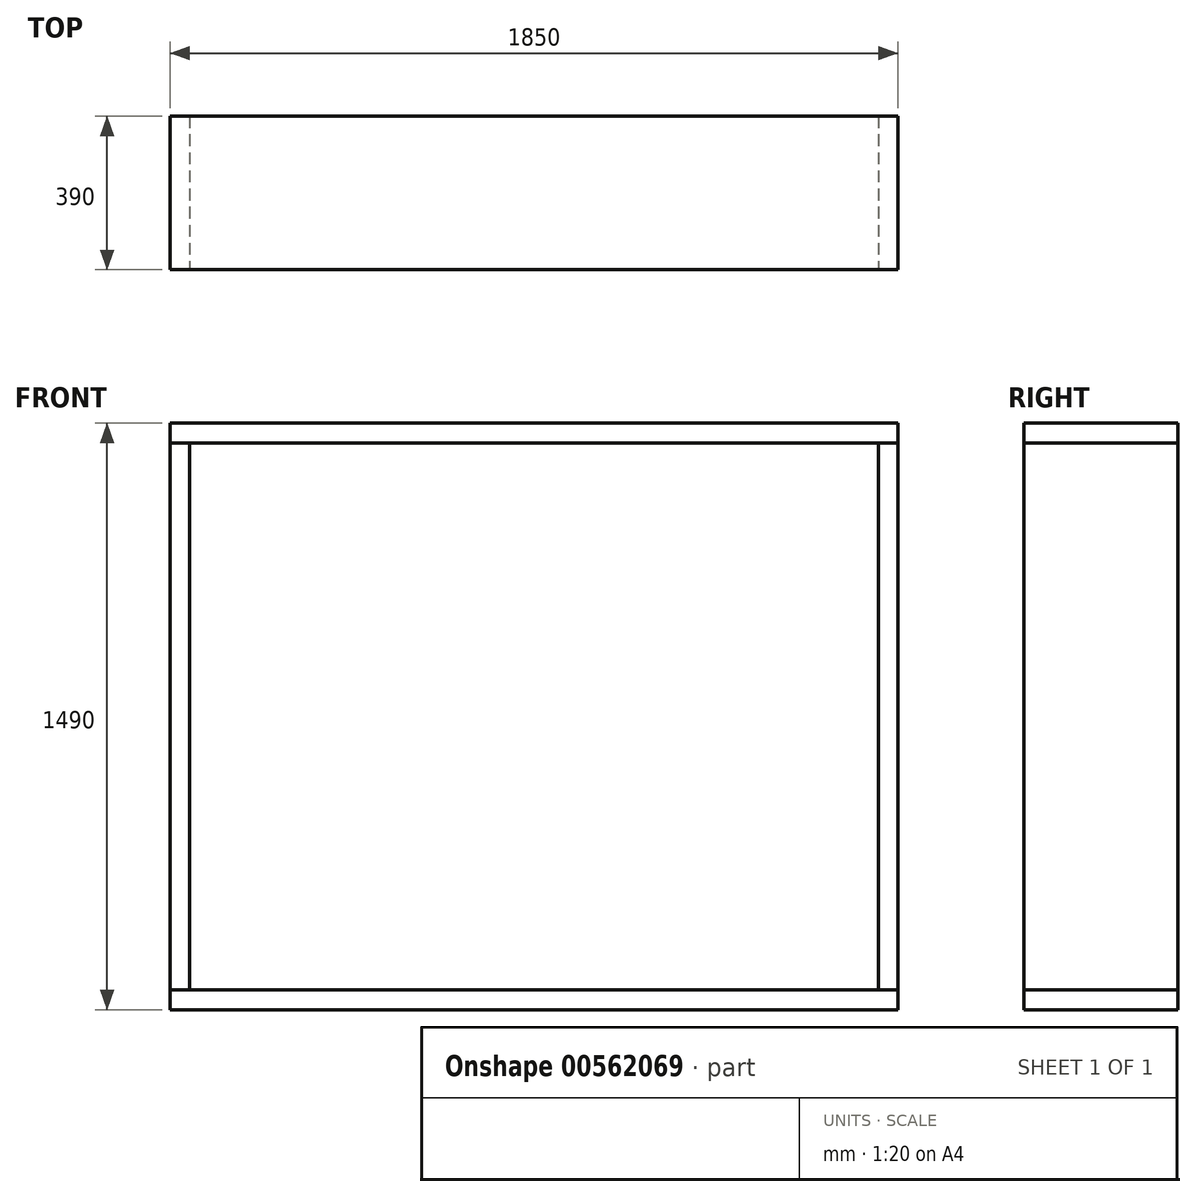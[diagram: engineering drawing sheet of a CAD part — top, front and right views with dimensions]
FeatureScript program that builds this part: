
annotation { "Feature Type Name" : "Feature", "Feature Type Description" : "" }
export const myFeature = defineFeature(function(context is Context, id is Id, definition is map)
    precondition{}
    {
        {
            var Q0;
            Q0=qCreatedBy(makeId("Top.planeOp"),FACE);
            var sketch = newSketch(context, id + "F0", { "sketchPlane" : qUnion([Q0])});
            skLineSegment(sketch, "E0.bottom", {"start": v(0, 0) * mm, "end": v(1850, 0) * mm});
            skLineSegment(sketch, "E0.top", {"start": v(0, -390) * mm, "end": v(1850, -390) * mm});
            skLineSegment(sketch, "E0.left", {"start": v(0, 0) * mm, "end": v(0, -390) * mm});
            skLineSegment(sketch, "E0.right", {"start": v(1850, 0) * mm, "end": v(1850, -390) * mm});
            skSolve(sketch);
        }
        {
            var Q0;
            Q0=makeQuery(id+"F0.imprint","IMPRINT",FACE,{"disambiguationData":[TD([[makeQuery(id+"F0.imprint","IMPRINT",EDGE,{"derivedFrom":sQuery(id+"F0.wireOp",EDGE,"E0.bottom")}),-1.0]])]});
            extrude(context, id + "F1", {"entities" : qUnion([Q0]), "depth" : 50 * mm, "offsetDistance" : 25 * mm});
        }
        {
            var Q0;
            Q0=makeQuery(id+"F1.opExtrude","SWEPT_FACE",FACE,{"disambiguationData":[OSD([sQuery(id+"F0.wireOp",EDGE,"E0.left")])]});
            var sketch = newSketch(context, id + "F2", { "sketchPlane" : qUnion([Q0])});
            skLineSegment(sketch, "E1.bottom", {"start": v(390, 50) * mm, "end": v(0, 50) * mm});
            skLineSegment(sketch, "E1.top", {"start": v(390, 1440) * mm, "end": v(0, 1440) * mm});
            skLineSegment(sketch, "E1.left", {"start": v(390, 50) * mm, "end": v(390, 1440) * mm});
            skLineSegment(sketch, "E1.right", {"start": v(0, 50) * mm, "end": v(0, 1440) * mm});
            skSolve(sketch);
        }
        {
            var Q0;
            Q0=makeQuery(id+"F2.imprint","IMPRINT",FACE,{"disambiguationData":[TD([[makeQuery(id+"F2.imprint","IMPRINT",EDGE,{"derivedFrom":sQuery(id+"F2.wireOp",EDGE,"E1.bottom")}),1.0]])]});
            extrude(context, id + "F3", {"entities" : qUnion([Q0]), "oppositeDirection" : true, "depth" : 50 * mm, "offsetDistance" : 25 * mm});
        }
        {
            var Q0;
            Q0=makeQuery(id+"F1.opExtrude","SWEPT_FACE",FACE,{"disambiguationData":[OSD([sQuery(id+"F0.wireOp",EDGE,"E0.right")])]});
            var sketch = newSketch(context, id + "F4", { "sketchPlane" : qUnion([Q0])});
            skLineSegment(sketch, "E2.bottom", {"start": v(-390, 50) * mm, "end": v(0, 50) * mm});
            skLineSegment(sketch, "E2.top", {"start": v(-390, 1440) * mm, "end": v(0, 1440) * mm});
            skLineSegment(sketch, "E2.left", {"start": v(-390, 50) * mm, "end": v(-390, 1440) * mm});
            skLineSegment(sketch, "E2.right", {"start": v(0, 50) * mm, "end": v(0, 1440) * mm});
            skSolve(sketch);
        }
        {
            var Q0;
            Q0=makeQuery(id+"F4.imprint","IMPRINT",FACE,{"disambiguationData":[TD([[makeQuery(id+"F4.imprint","IMPRINT",EDGE,{"derivedFrom":sQuery(id+"F4.wireOp",EDGE,"E2.bottom")}),-1.0]])]});
            extrude(context, id + "F5", {"entities" : qUnion([Q0]), "oppositeDirection" : true, "depth" : 50 * mm, "offsetDistance" : 25 * mm});
        }
        {
            var Q0;
            Q0=makeQuery(id+"F3.opExtrude","SWEPT_FACE",FACE,{"disambiguationData":[OSD([sQuery(id+"F2.wireOp",EDGE,"E1.top")])]});
            var sketch = newSketch(context, id + "F6", { "sketchPlane" : qUnion([Q0])});
            skLineSegment(sketch, "E3.bottom", {"start": v(0, 0) * mm, "end": v(1850, 0) * mm});
            skLineSegment(sketch, "E3.top", {"start": v(0, -390) * mm, "end": v(1850, -390) * mm});
            skLineSegment(sketch, "E3.left", {"start": v(0, 0) * mm, "end": v(0, -390) * mm});
            skLineSegment(sketch, "E3.right", {"start": v(1850, 0) * mm, "end": v(1850, -390) * mm});
            skSolve(sketch);
        }
        {
            var Q0;
            {var subQ0=sQuery(id+"F6.wireOp",EDGE,"E3.left");Q0=makeQuery(id+"F6.imprint","IMPRINT",FACE,{"disambiguationData":[TD([[makeQuery(id+"F6.imprint","IMPRINT",EDGE,{"derivedFrom":subQ0}),-1.0]])]});}
            var Q1;
            {var subQ2=sQuery(id+"F6.wireOp",EDGE,"E3.right");Q1=makeQuery(id+"F6.imprint","IMPRINT",FACE,{"disambiguationData":[TD([[makeQuery(id+"F6.imprint","IMPRINT",EDGE,{"derivedFrom":subQ2}),-1.0]])]});}
            extrude(context, id + "F7", {"entities" : qUnion([Q0, Q1]), "depth" : 50 * mm, "offsetDistance" : 25 * mm});
        }
    });
